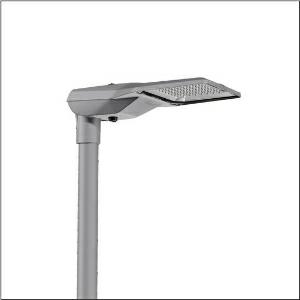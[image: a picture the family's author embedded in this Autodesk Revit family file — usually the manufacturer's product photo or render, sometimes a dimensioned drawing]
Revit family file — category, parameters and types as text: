
# Revit family: streetlight_sl_21_midi___st1_5a_5xe3p33t08lb_3dd1
name_source: partatom
category: Lighting Fixtures
units: mm (PartAtom-declared; Revit-internal decimal feet)

## family parameters
Cut with Voids When Loaded = No
Host = Face
Light Source = No
Part Type = Normal
Room Calculation Point = No
Round Connector Dimension = Use Diameter
Shared = No

## types (1)
- --- (1 x LED, 14100 lm, 99.6 W, 3000K)
    Apparent Load = 100 VA
    CIE Flux Codes = 22 53 95 100 100
    Color Rendering = 70
    Color Temperature = 3000K
    Default Elevation = 1800 mm
    Description = Streetlight SL 21 midi, mast luminaire, primary light control with lens, of PMMA, primary optical cover: cover, of toughened safety glass, transparent, light distribution: ST1.5a, light emission: direct distribution, primary light characteristic: asymmetric, installation type: side-entry, post-top, LED, High Power LED, rated luminous flux: 14.100lm, luminous efficacy: 142lm/W, light colour: 730, colour temperature: 3000K, control gear: D4i, control: overheat protection, constant luminous flux control, time-dependent luminous flux control, flexible luminous flux parameterisation, pre-setting: logarithmic dimming characteristic, mains connection: 230..240V, AC, 50/60Hz, start of lifetime: 100W, end of service life: 102W, reduction: 46W, luminaire housing, of diecast aluminium, powder-coated, Siteco® metallic grey (DB 702S), corrosivity category C5 mid according to DIN EN ISO 12944, please order mast flange separately, inclination adjustable: 0°, 5°, 10°, 15°, sealing non-destructively replaceable, multi-level sealing system, length: 644mm, width: 335mm, height: 110mm, mast flange for spigot size: 42mm (side-entry): 5XC10008XM4, 60/48mm (side-entry/post-top): 5XC10108XM2, 76/60mm (side-entry/post-top): 5XC10108XM1, mounting height: 4..8m, Smart Interface below and above, protection rating (complete): IP66, insulation class (complete): insulation class II (safety insulation), certification: CE, ENEC, ENEC+, VDE, impact resistance: IK10, permissible operating ambient temperature for outdoor applications: -40..+50°C, standard-compliant lighting for roads and squares, packaging unit: 1 piece

Light Distribution: ST1.5a
    Height = 111 mm
    Lamp = 1 x LED
    Lamp Light Flux = 14100 lm
    Lamp Power = 99.6 W
    Lamp count = 1
    Length = 644 mm
    Luminous efficacy = 142 lm/W
    Manufacturer = Siteco
    ModVariant = No
    Model = 5XE3P33T08LB
    Number of Poles = 1
    OnlyDefault = Yes
    Power Factor = 1
    Product Name = Streetlight SL 21 midi | ST1.5a
    Product group = mast luminaire | pylon top
    ProductGroupID = 6100
    Protection Class = Protection class II
    Protection Degree = IP 66
    RLX_Detail_Level = 1
    RLX_Emergency_Light_Flux = 0 lm
    RLX_Emergency_Type = 0
    RLX_Emergency_Type_DB = No
    RlxData = <blob elided: 30489 chars, md5=d6934ebc>
    Socket = socket
    Standby Power = 0 W
    System Light Flux = 14100 lm
    System Power = 100 W
    Type Comments = factory setting: luminous flux: 100 % | dim-lin: 254 | 1020 mA
    Type Image = l_1004304.jpg
    URL = http://relux.com
    VarID = @adj_012859
    Voltage = 0 V
    Weight = 0.00 kg
    Width = 336 mm

## geometry (parser evidence)
native form markers: Blend x4, Sweep x11
no freeform markers — native parametric forms only
